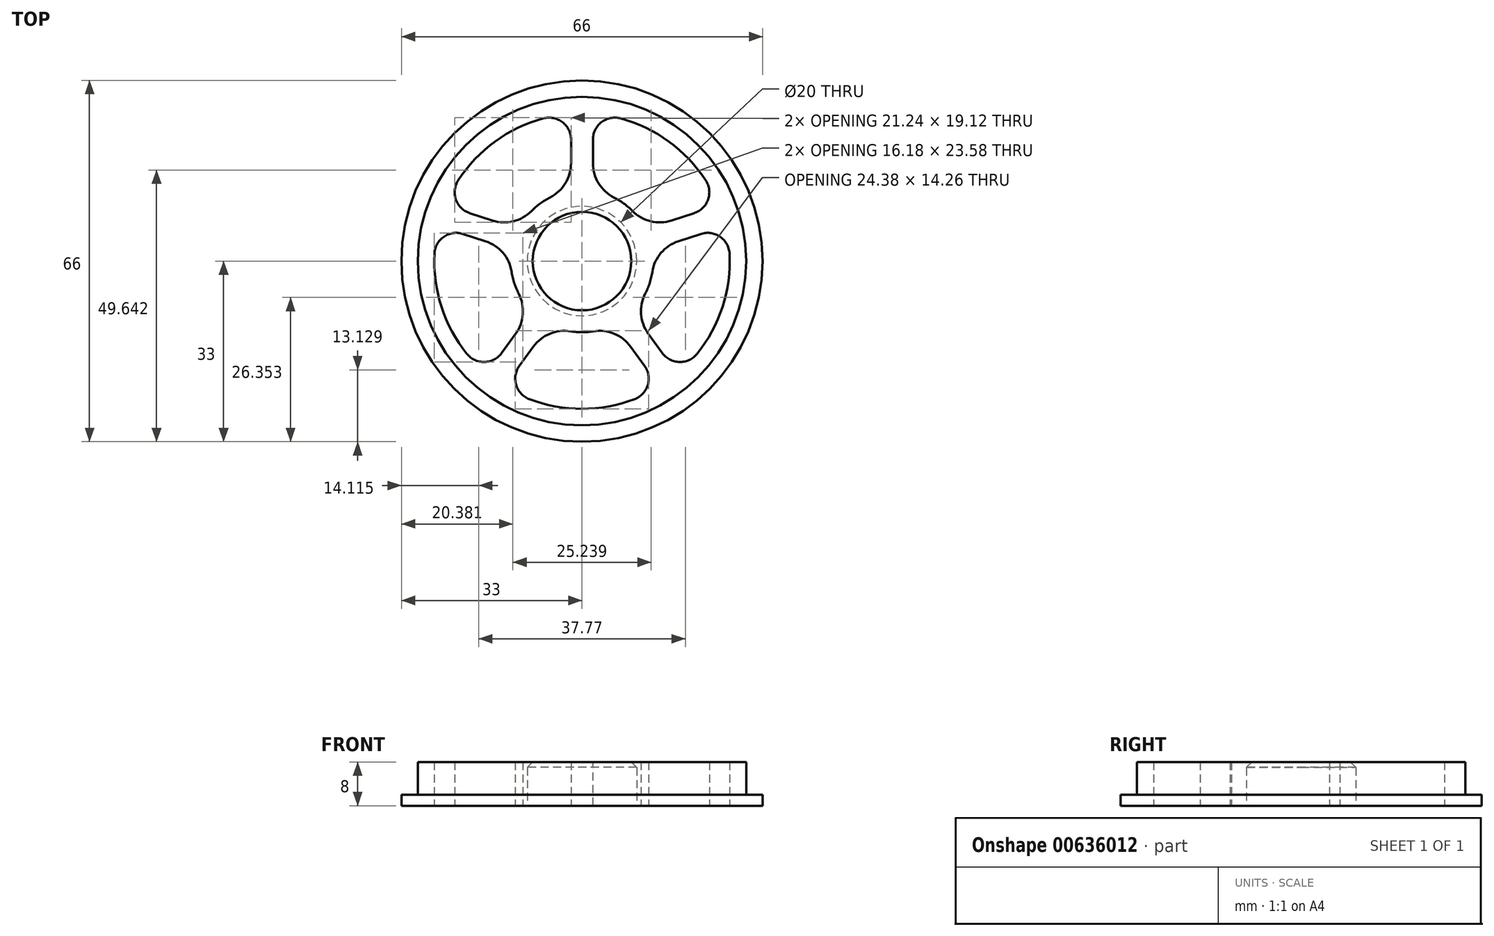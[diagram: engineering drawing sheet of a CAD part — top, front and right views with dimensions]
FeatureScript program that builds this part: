
annotation { "Feature Type Name" : "Feature", "Feature Type Description" : "" }
export const myFeature = defineFeature(function(context is Context, id is Id, definition is map)
    precondition{}
    {
        {
            var Q0;
            Q0=qCreatedBy(makeId("Top.planeOp"),FACE);
            var sketch = newSketch(context, id + "F0", { "sketchPlane" : qUnion([Q0])});
            skCircle(sketch, "E0", {"center": v(0, 0) * mm, "radius": 10 * mm});
            skCircle(sketch, "E1", {"center": v(0, 0) * mm, "radius": 30 * mm});
            skArc(sketch, "E2.0", {"start": v(-2, 12.85) * mm, "mid": v(-7.64, 10.52) * mm, "end": v(-11.6, 5.87) * mm});
            skArc(sketch, "E3.0", {"start": v(-2, 26.93) * mm, "mid": v(-15.87, 21.84) * mm, "end": v(-24.99, 10.22) * mm});
            skLineSegment(sketch, "E4", {"start": v(0, 13) * mm, "end": v(0, 27) * mm, "construction": true});
            skLineSegment(sketch, "E5.0", {"start": v(2, 12.85) * mm, "end": v(2, 26.93) * mm});
            skLineSegment(sketch, "E6.0", {"start": v(-2, 12.85) * mm, "end": v(-2, 26.93) * mm});
            skLineSegment(sketch, "E7.1.0", {"start": v(-11.6, 5.87) * mm, "end": v(-24.99, 10.22) * mm});
            skLineSegment(sketch, "E7.1.1", {"start": v(-12.83, 2.07) * mm, "end": v(-26.23, 6.42) * mm});
            skLineSegment(sketch, "E7.2.0", {"start": v(-9.17, -9.22) * mm, "end": v(-17.44, -20.6) * mm});
            skLineSegment(sketch, "E7.2.1", {"start": v(-5.93, -11.57) * mm, "end": v(-14.2, -22.96) * mm});
            skLineSegment(sketch, "E8.1.3.0", {"start": v(5.93, -11.57) * mm, "end": v(14.2, -22.96) * mm});
            skLineSegment(sketch, "E8.3.3.0", {"start": v(9.17, -9.22) * mm, "end": v(17.44, -20.6) * mm});
            skLineSegment(sketch, "E8.1.4.0", {"start": v(12.83, 2.07) * mm, "end": v(26.23, 6.42) * mm});
            skLineSegment(sketch, "E8.3.4.0", {"start": v(11.6, 5.87) * mm, "end": v(24.99, 10.22) * mm});
            skArc(sketch, "E9.trimOffspring", {"start": v(-26.23, 6.42) * mm, "mid": v(-25.68, -8.34) * mm, "end": v(-17.44, -20.6) * mm});
            skArc(sketch, "E10.trimOffspring", {"start": v(-12.83, 2.07) * mm, "mid": v(-12.36, -4.02) * mm, "end": v(-9.17, -9.22) * mm});
            skArc(sketch, "E11.trimOffspring", {"start": v(11.6, 5.87) * mm, "mid": v(7.64, 10.52) * mm, "end": v(2, 12.85) * mm});
            skArc(sketch, "E12.trimOffspring", {"start": v(9.17, -9.22) * mm, "mid": v(12.36, -4.02) * mm, "end": v(12.83, 2.07) * mm});
            skArc(sketch, "E13.trimOffspring", {"start": v(-5.93, -11.57) * mm, "mid": v(0, -13) * mm, "end": v(5.93, -11.57) * mm});
            skArc(sketch, "E14.trimOffspring", {"start": v(-14.2, -22.96) * mm, "mid": v(0, -27) * mm, "end": v(14.2, -22.96) * mm});
            skArc(sketch, "E15.trimOffspring", {"start": v(17.44, -20.6) * mm, "mid": v(25.68, -8.34) * mm, "end": v(26.23, 6.42) * mm});
            skArc(sketch, "E16.trimOffspring", {"start": v(24.99, 10.22) * mm, "mid": v(15.87, 21.84) * mm, "end": v(2, 26.93) * mm});
            skSolve(sketch);
        }
        {
            var Q0;
            Q0 = qSketchRegion(id + "F0", true);
            extrude(context, id + "F1", {"entities" : qUnion([Q0]), "depth" : 8 * mm, "offsetDistance" : 25 * mm});
        }
        {
            var Q0;
            Q0=makeQuery(id+"F1.opExtrude","CAP_FACE",FACE,{"disambiguationData":[OSD([sQuery(id+"F0.wireOp",EDGE,"E0"),sQuery(id+"F0.wireOp",EDGE,"E1"),sQuery(id+"F0.wireOp",EDGE,"E2.0"),sQuery(id+"F0.wireOp",EDGE,"E3.0"),sQuery(id+"F0.wireOp",EDGE,"E5.0"),sQuery(id+"F0.wireOp",EDGE,"E6.0"),sQuery(id+"F0.wireOp",EDGE,"E7.1.0"),sQuery(id+"F0.wireOp",EDGE,"E7.1.1"),sQuery(id+"F0.wireOp",EDGE,"E7.2.0"),sQuery(id+"F0.wireOp",EDGE,"E7.2.1"),sQuery(id+"F0.wireOp",EDGE,"E8.1.3.0"),sQuery(id+"F0.wireOp",EDGE,"E8.3.3.0"),sQuery(id+"F0.wireOp",EDGE,"E8.1.4.0"),sQuery(id+"F0.wireOp",EDGE,"E8.3.4.0"),sQuery(id+"F0.wireOp",EDGE,"E9.trimOffspring"),sQuery(id+"F0.wireOp",EDGE,"E10.trimOffspring"),sQuery(id+"F0.wireOp",EDGE,"E11.trimOffspring"),sQuery(id+"F0.wireOp",EDGE,"E12.trimOffspring"),sQuery(id+"F0.wireOp",EDGE,"E13.trimOffspring"),sQuery(id+"F0.wireOp",EDGE,"E14.trimOffspring"),sQuery(id+"F0.wireOp",EDGE,"E15.trimOffspring"),sQuery(id+"F0.wireOp",EDGE,"E16.trimOffspring")])],"isStart":true});
            var sketch = newSketch(context, id + "F2", { "sketchPlane" : qUnion([Q0])});
            skCircle(sketch, "E17.0", {"center": v(0, 0) * mm, "radius": 30 * mm});
            skCircle(sketch, "E18.0", {"center": v(0, 0) * mm, "radius": 33 * mm});
            skSolve(sketch);
        }
        {
            var Q0;
            Q0 = qSketchRegion(id + "F2", true);
            extrude(context, id + "F3", {"entities" : qUnion([Q0]), "operationType" : NewBodyOperationType.ADD, "oppositeDirection" : true, "depth" : 2 * mm, "offsetDistance" : 25 * mm});
        }
        {
            var Q0;
            Q0=makeQuery(id+"F1.opExtrude","CAP_FACE",FACE,{"disambiguationData":[OSD([sQuery(id+"F0.wireOp",EDGE,"E0"),sQuery(id+"F0.wireOp",EDGE,"E1"),sQuery(id+"F0.wireOp",EDGE,"E2.0"),sQuery(id+"F0.wireOp",EDGE,"E3.0"),sQuery(id+"F0.wireOp",EDGE,"E5.0"),sQuery(id+"F0.wireOp",EDGE,"E6.0"),sQuery(id+"F0.wireOp",EDGE,"E7.1.0"),sQuery(id+"F0.wireOp",EDGE,"E7.1.1"),sQuery(id+"F0.wireOp",EDGE,"E7.2.0"),sQuery(id+"F0.wireOp",EDGE,"E7.2.1"),sQuery(id+"F0.wireOp",EDGE,"E8.1.3.0"),sQuery(id+"F0.wireOp",EDGE,"E8.3.3.0"),sQuery(id+"F0.wireOp",EDGE,"E8.1.4.0"),sQuery(id+"F0.wireOp",EDGE,"E8.3.4.0"),sQuery(id+"F0.wireOp",EDGE,"E9.trimOffspring"),sQuery(id+"F0.wireOp",EDGE,"E10.trimOffspring"),sQuery(id+"F0.wireOp",EDGE,"E11.trimOffspring"),sQuery(id+"F0.wireOp",EDGE,"E12.trimOffspring"),sQuery(id+"F0.wireOp",EDGE,"E13.trimOffspring"),sQuery(id+"F0.wireOp",EDGE,"E14.trimOffspring"),sQuery(id+"F0.wireOp",EDGE,"E15.trimOffspring"),sQuery(id+"F0.wireOp",EDGE,"E16.trimOffspring")])],"isStart":false});
            var sketch = newSketch(context, id + "F4", { "sketchPlane" : qUnion([Q0])});
            skCircle(sketch, "E19.0", {"center": v(0, 0) * mm, "radius": 10 * mm});
            skCircle(sketch, "E20.0", {"center": v(0, 0) * mm, "radius": 9 * mm});
            skSolve(sketch);
        }
        {
            var Q0;
            Q0 = qSketchRegion(id + "F4", true);
            extrude(context, id + "F5", {"entities" : qUnion([Q0]), "operationType" : NewBodyOperationType.ADD, "oppositeDirection" : true, "depth" : 1 * mm, "offsetDistance" : 25 * mm});
        }
        {
            var Q0;
            Q0=makeQuery(id+"F1.opExtrude","SWEPT_EDGE",EDGE,{"disambiguationData":[OSD([sQuery(id+"F0.wireOp",EDGE,"E7.1.1"),sQuery(id+"F0.wireOp",EDGE,"E9.trimOffspring")])]});
            var Q1;
            Q1=makeQuery(id+"F1.opExtrude","SWEPT_EDGE",EDGE,{"disambiguationData":[OSD([sQuery(id+"F0.wireOp",EDGE,"E3.0"),sQuery(id+"F0.wireOp",EDGE,"E7.1.0")])]});
            var Q2;
            Q2=makeQuery(id+"F1.opExtrude","SWEPT_EDGE",EDGE,{"disambiguationData":[OSD([sQuery(id+"F0.wireOp",EDGE,"E7.2.0"),sQuery(id+"F0.wireOp",EDGE,"E9.trimOffspring")])]});
            var Q3;
            Q3=makeQuery(id+"F1.opExtrude","SWEPT_EDGE",EDGE,{"disambiguationData":[OSD([sQuery(id+"F0.wireOp",EDGE,"E8.3.3.0"),sQuery(id+"F0.wireOp",EDGE,"E15.trimOffspring")])]});
            var Q4;
            Q4=makeQuery(id+"F1.opExtrude","SWEPT_EDGE",EDGE,{"disambiguationData":[OSD([sQuery(id+"F0.wireOp",EDGE,"E8.1.4.0"),sQuery(id+"F0.wireOp",EDGE,"E15.trimOffspring")])]});
            var Q5;
            Q5=makeQuery(id+"F1.opExtrude","SWEPT_EDGE",EDGE,{"disambiguationData":[OSD([sQuery(id+"F0.wireOp",EDGE,"E3.0"),sQuery(id+"F0.wireOp",EDGE,"E6.0")])]});
            var Q6;
            Q6=makeQuery(id+"F1.opExtrude","SWEPT_EDGE",EDGE,{"disambiguationData":[OSD([sQuery(id+"F0.wireOp",EDGE,"E7.2.1"),sQuery(id+"F0.wireOp",EDGE,"E14.trimOffspring")])]});
            var Q7;
            Q7=makeQuery(id+"F1.opExtrude","SWEPT_EDGE",EDGE,{"disambiguationData":[OSD([sQuery(id+"F0.wireOp",EDGE,"E8.1.3.0"),sQuery(id+"F0.wireOp",EDGE,"E14.trimOffspring")])]});
            var Q8;
            Q8=makeQuery(id+"F1.opExtrude","SWEPT_EDGE",EDGE,{"disambiguationData":[OSD([sQuery(id+"F0.wireOp",EDGE,"E8.3.4.0"),sQuery(id+"F0.wireOp",EDGE,"E16.trimOffspring")])]});
            var Q9;
            Q9=makeQuery(id+"F1.opExtrude","SWEPT_EDGE",EDGE,{"disambiguationData":[OSD([sQuery(id+"F0.wireOp",EDGE,"E5.0"),sQuery(id+"F0.wireOp",EDGE,"E16.trimOffspring")])]});
            fillet(context, id + "F6", {"entities" : qUnion([Q0, Q1, Q2, Q3, Q4, Q5, Q6, Q7, Q8, Q9]), "radius" : 4 * mm, "tangentPropagation" : true, "allowEdgeOverflow" : false});
        }
        {
            var Q0;
            Q0=makeQuery(id+"F1.opExtrude","SWEPT_EDGE",EDGE,{"disambiguationData":[OSD([sQuery(id+"F0.wireOp",EDGE,"E7.1.1"),sQuery(id+"F0.wireOp",EDGE,"E10.trimOffspring")])]});
            var Q1;
            Q1=makeQuery(id+"F1.opExtrude","SWEPT_EDGE",EDGE,{"disambiguationData":[OSD([sQuery(id+"F0.wireOp",EDGE,"E7.2.0"),sQuery(id+"F0.wireOp",EDGE,"E10.trimOffspring")])]});
            var Q2;
            Q2=makeQuery(id+"F1.opExtrude","SWEPT_EDGE",EDGE,{"disambiguationData":[OSD([sQuery(id+"F0.wireOp",EDGE,"E7.2.1"),sQuery(id+"F0.wireOp",EDGE,"E13.trimOffspring")])]});
            var Q3;
            Q3=makeQuery(id+"F1.opExtrude","SWEPT_EDGE",EDGE,{"disambiguationData":[OSD([sQuery(id+"F0.wireOp",EDGE,"E8.1.3.0"),sQuery(id+"F0.wireOp",EDGE,"E13.trimOffspring")])]});
            var Q4;
            Q4=makeQuery(id+"F1.opExtrude","SWEPT_EDGE",EDGE,{"disambiguationData":[OSD([sQuery(id+"F0.wireOp",EDGE,"E8.3.3.0"),sQuery(id+"F0.wireOp",EDGE,"E12.trimOffspring")])]});
            var Q5;
            Q5=makeQuery(id+"F1.opExtrude","SWEPT_EDGE",EDGE,{"disambiguationData":[OSD([sQuery(id+"F0.wireOp",EDGE,"E8.1.4.0"),sQuery(id+"F0.wireOp",EDGE,"E12.trimOffspring")])]});
            var Q6;
            Q6=makeQuery(id+"F1.opExtrude","SWEPT_EDGE",EDGE,{"disambiguationData":[OSD([sQuery(id+"F0.wireOp",EDGE,"E8.3.4.0"),sQuery(id+"F0.wireOp",EDGE,"E11.trimOffspring")])]});
            var Q7;
            Q7=makeQuery(id+"F1.opExtrude","SWEPT_EDGE",EDGE,{"disambiguationData":[OSD([sQuery(id+"F0.wireOp",EDGE,"E5.0"),sQuery(id+"F0.wireOp",EDGE,"E11.trimOffspring")])]});
            var Q8;
            Q8=makeQuery(id+"F1.opExtrude","SWEPT_EDGE",EDGE,{"disambiguationData":[OSD([sQuery(id+"F0.wireOp",EDGE,"E2.0"),sQuery(id+"F0.wireOp",EDGE,"E6.0")])]});
            var Q9;
            Q9=makeQuery(id+"F1.opExtrude","SWEPT_EDGE",EDGE,{"disambiguationData":[OSD([sQuery(id+"F0.wireOp",EDGE,"E2.0"),sQuery(id+"F0.wireOp",EDGE,"E7.1.0")])]});
            fillet(context, id + "F7", {"entities" : qUnion([Q0, Q1, Q2, Q3, Q4, Q5, Q6, Q7, Q8, Q9]), "radius" : 7 * mm, "tangentPropagation" : true, "allowEdgeOverflow" : false});
        }
        {
            var Q0;
            Q0=makeQuery(id+"F5.opExtrude","CAP_EDGE",EDGE,{"disambiguationData":[OSD([sQuery(id+"F4.wireOp",EDGE,"E20.0")])],"isStart":false});
            chamfer(context, id + "F8", {"entities" : qUnion([Q0]), "width" : 1 * mm, "tangentPropagation" : true});
        }
    });
